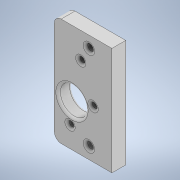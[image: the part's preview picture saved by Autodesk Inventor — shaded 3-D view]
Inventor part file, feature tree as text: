
AUTODESK INVENTOR PART (.ipt)
format: ipt  version: 2020 (Build 240168000, 168)  size: 168,960 bytes
history: native  units: in
note: dims shown in document units (in); Inventor stores cm internally (conversion verified against a paired STEP export)
features: fillet x2, extrude x1, sketch x1
ambient origin geometry x8: Origin, YZ Plane, XZ Plane, XY Plane, X Axis, Y Axis, Z Axis, Center Point
bodies: Solid1 (feature_tree)
feature tree (4):
  extrude  "Extrusion1"  Depth=0.0394in
  fillet  "Fillet1"  Radius=0.1181in
  fillet  "Fillet2"  [1 undecoded]
  sketch  "Sketch1"  dims[d8=0.2362in d9=0.0in d10=0.0394in d11=0.1181in]
note: 1 required parameter value undecoded (feature->parameter linkage not recoverable at this tier; creation-order binding heuristic only, values carry confidence <= 0.55)
